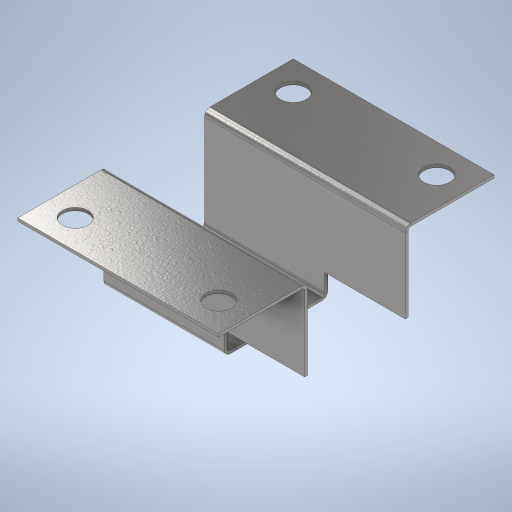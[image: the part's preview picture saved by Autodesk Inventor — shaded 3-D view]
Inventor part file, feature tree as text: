
AUTODESK INVENTOR PART (.ipt)
format: ipt  version: 2024 (Build 280153000, 153)  size: 381,952 bytes
history: native  units: mm
features: other x19, sketch x8, hole x2, projected_geometry x1
ambient origin geometry x8: Origin, YZ Plane, XZ Plane, XY Plane, X Axis, Y Axis, Z Axis, Center Point
bodies: Body1 (feature_tree)
feature tree (30):
  other  "Fläche2"
  other  "Lasche1"
  other  "Lasche2"
  other  "Lasche3"
  other  "Lasche4"
  hole  "Bohrung1"  [1 undecoded]
  hole  "Bohrung2"  [1 undecoded]
  sketch  "Skizze2"  dims[d3=2.0mm d12=18.0mm]
  other  "Grobblech2"
  sketch  "Skizze3"  dims[d13=35.0mm d14=0.5mm]
  other  "Grobblech3"
  other  "Biegung1"
  other  "Ecke1"
  sketch  "Skizze4"  dims[d15=0.5mm]
  other  "Grobblech4"
  other  "Biegung2"
  other  "Ecke2"
  sketch  "Skizze5"  dims[d16=0.25mm]
  other  "Grobblech5"
  other  "Biegung3"
  other  "Ecke3"
  sketch  "Skizze6"  dims[d17=1.0mm]
  other  "Grobblech6"
  other  "Biegung4"
  other  "Ecke4"
  sketch  "Skizze7"  dims[d18=0.5mm]
  sketch  "Skizze8"  dims[d19=18.0mm d20=90.0deg d21=0.5mm]
  projected_geometry  "Projizierte Kontur1"
  sketch  "Skizze9"  dims[d22=2.0mm d23=0.5mm d24=0.5mm d25=0.5mm d26=0.25mm d27=1.0mm d28=0.5mm d29=18.0mm d30=90.0deg d31=0.5mm d32=2.0mm d33=0.5mm d34=0.5mm d35=0.5mm d36=0.25mm d37=1.0mm d38=0.5mm d39=15.5mm d40=90.0deg d41=0.5mm d42=2.0mm d43=0.5mm d44=0.5mm d45=0.5mm d46=0.25mm d47=1.0mm d48=0.5mm d49=15.5mm d50=90.0deg d51=0.5mm d52=2.0mm d53=0.5mm d54=0.5mm d55=4.0mm d56=14.0mm d57=0.5mm d58=0.0mm d59=25.0mm d60=38.0mm d61=25.0mm d62=38.0mm d63=4.5mm d64=6.0mm d65=4.0mm d66=2.0mm d67=90.0deg d68=0.5mm d69=20.594885mm d70=8.0mm d71=8.0mm d72=3.0mm d73=6.0mm d74=4.0mm d75=2.0mm d76=90.0deg d77=8.0mm d78=20.594885mm]
  other  "Ausschneiden1"
note: 2 required parameter values undecoded (feature->parameter linkage not recoverable at this tier; creation-order binding heuristic only, values carry confidence <= 0.55)
